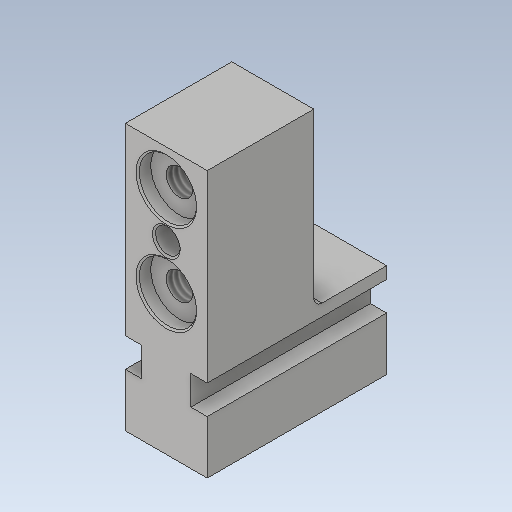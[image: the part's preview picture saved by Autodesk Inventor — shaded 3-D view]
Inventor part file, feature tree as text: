
AUTODESK INVENTOR PART (.ipt)
format: ipt  version: 2020 (Build 240168000, 168)  size: 186,880 bytes
history: native  units: mm
features: other x21, sketch x6, extrude x3, revolve x3, thread x2
ambient origin geometry x8: Origin, YZ Plane, XZ Plane, XY Plane, X Axis, Y Axis, Z Axis, Center Point
bodies: Solid1 (feature_tree)
feature tree (35):
  extrude  "Extrusion1"  Depth=10.0mm TaperAngle=0.0deg
  extrude  "Extrusion2"  TaperAngle=360.0deg  [1 undecoded]
  revolve  "Revolution1"  Angle=360.0deg
  revolve  "Revolution2"  [1 undecoded]
  thread  "Thread1"  [1 undecoded]
  revolve  "Revolution3"  [1 undecoded]
  thread  "Thread2"  [1 undecoded]
  extrude  "Extrusion3"  [1 undecoded]
  other  "GRIFF_XY"
  other  "GRIFF_YZ"
  other  "GRIFF_ZX"
  other  "GRIFF_X"
  other  "GRIFF_Y"
  other  "GRIFF_Z"
  other  "GRIFF_Center"
  other  "TO_ZBH_1_XY"
  other  "TO_ZBH_1_YZ"
  other  "TO_ZBH_1_ZX"
  other  "TO_ZBH_1_X"
  other  "TO_ZBH_1_Y"
  other  "TO_ZBH_1_Z"
  other  "TO_ZBH_1_Center"
  other  "TO_ZBH_2_XY"
  other  "TO_ZBH_2_YZ"
  other  "TO_ZBH_2_ZX"
  other  "TO_ZBH_2_X"
  other  "TO_ZBH_2_Y"
  other  "TO_ZBH_2_Z"
  other  "TO_ZBH_2_Center"
  sketch  "Sketch_1"  dims[d0=21.9mm d1=0.0mm d2=10.0mm d3=0.0mm]
  sketch  "Sketch_2"  dims[d4=360.0deg d5=360.0deg]
  sketch  "Sketch_5"  dims[d6=11.4mm d7=0.0mm d8=360.0deg]
  sketch  "Sketch_6"  dims[d9=11.4mm d10=0.0mm d11=1.5mm d12=0.0mm d13=0.0mm d14=0.0mm d15=0.0mm]
  sketch  "Sketch_7"
  sketch  "Sketch_10"
note: 6 required parameter values undecoded (feature->parameter linkage not recoverable at this tier; creation-order binding heuristic only, values carry confidence <= 0.55)